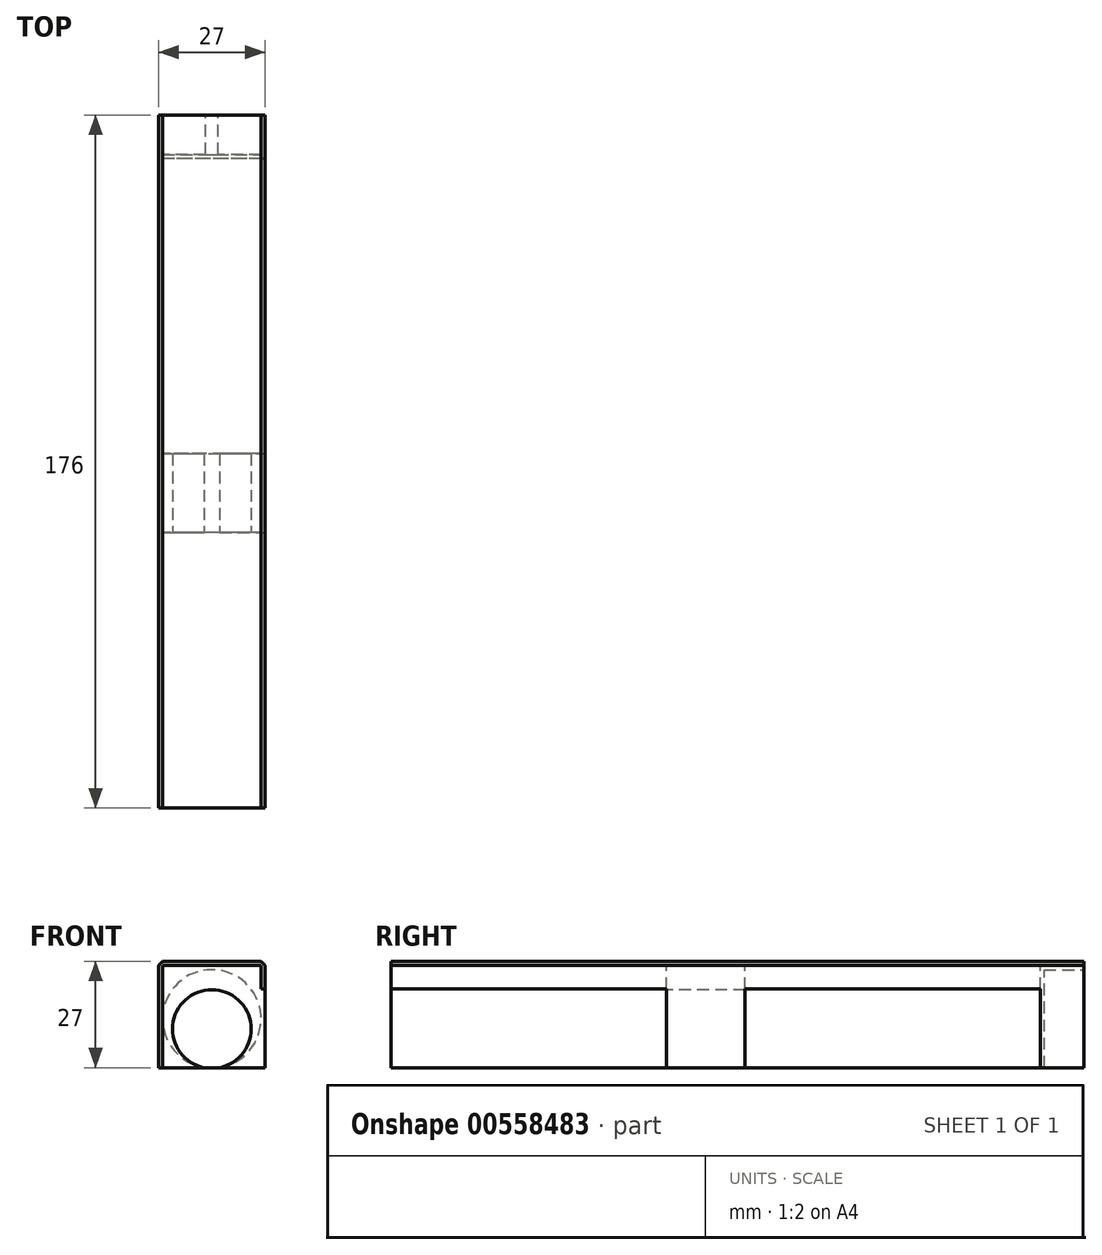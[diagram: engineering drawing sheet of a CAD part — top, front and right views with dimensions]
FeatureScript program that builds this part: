
annotation { "Feature Type Name" : "Feature", "Feature Type Description" : "" }
export const myFeature = defineFeature(function(context is Context, id is Id, definition is map)
    precondition{}
    {
        {
            var Q0;
            Q0=qCreatedBy(makeId("Front.planeOp"),FACE);
            var sketch = newSketch(context, id + "F0", { "sketchPlane" : qUnion([Q0])});
            skLineSegment(sketch, "E0", {"start": v(0, 0) * mm, "end": v(0, 27) * mm});
            skLineSegment(sketch, "E1", {"start": v(0, 27) * mm, "end": v(13.5, 27) * mm});
            skLineSegment(sketch, "E2", {"start": v(13.5, 27) * mm, "end": v(13.5, 26) * mm});
            skLineSegment(sketch, "E3", {"start": v(13.5, 26) * mm, "end": v(1, 26) * mm});
            skLineSegment(sketch, "E4", {"start": v(1, 26) * mm, "end": v(1, 0) * mm});
            skLineSegment(sketch, "E5", {"start": v(1, 0) * mm, "end": v(0, 0) * mm});
            skSolve(sketch);
        }
        {
            var Q0;
            Q0 = qSketchRegion(id + "F0", true);
            extrude(context, id + "F1", {"entities" : qUnion([Q0]), "depth" : 176 * mm, "offsetDistance" : 25 * mm});
        }
        {
            var Q0;
            Q0=makeQuery(id+"F1.opExtrude","SWEPT_BODY",BODY,{"disambiguationData":[OSD([sQuery(id+"F0.wireOp",EDGE,"E0"),sQuery(id+"F0.wireOp",EDGE,"E1"),sQuery(id+"F0.wireOp",EDGE,"E2"),sQuery(id+"F0.wireOp",EDGE,"E3"),sQuery(id+"F0.wireOp",EDGE,"E4"),sQuery(id+"F0.wireOp",EDGE,"E5")])]});
            var Q1;
            Q1=makeQuery(id+"F1.opExtrude","SWEPT_FACE",FACE,{"disambiguationData":[OSD([sQuery(id+"F0.wireOp",EDGE,"E2")])]});
            mirror(context, id + "F2", {"operationType" : NewBodyOperationType.ADD, "entities" : qUnion([Q0]), "mirrorPlane" : qUnion([Q1])});
        }
        {
            var Q0;
            {var subQ0=makeQuery(id+"F1.opExtrude","SWEPT_FACE",FACE,{"disambiguationData":[OSD([sQuery(id+"F0.wireOp",EDGE,"E3")])]});Q0=makeQuery(id+"F2.boolean.opBoolean","MERGE",FACE,{"derivedFrom":[subQ0,makeQuery(id+"F2.opPattern","COPY",FACE,{"derivedFrom":subQ0,"instanceName":"1"})]});}
            var sketch = newSketch(context, id + "F3", { "sketchPlane" : qUnion([Q0])});
            skLineSegment(sketch, "E6.bottom", {"start": v(26, 10) * mm, "end": v(1, 10) * mm});
            skLineSegment(sketch, "E6.top", {"start": v(26, 11) * mm, "end": v(1, 11) * mm});
            skLineSegment(sketch, "E6.left", {"start": v(26, 10) * mm, "end": v(26, 11) * mm});
            skLineSegment(sketch, "E6.right", {"start": v(1, 10) * mm, "end": v(1, 11) * mm});
            skSolve(sketch);
        }
        {
            var Q0;
            Q0 = qSketchRegion(id + "F3", true);
            var Q1;
            Q1=qCreatedBy(makeId("Front.planeOp"),FACE);
            var Q2;
            Q2=makeQuery(id+"F1.opExtrude","SWEPT_BODY",BODY,{"disambiguationData":[OSD([sQuery(id+"F0.wireOp",EDGE,"E0"),sQuery(id+"F0.wireOp",EDGE,"E1"),sQuery(id+"F0.wireOp",EDGE,"E2"),sQuery(id+"F0.wireOp",EDGE,"E3"),sQuery(id+"F0.wireOp",EDGE,"E4"),sQuery(id+"F0.wireOp",EDGE,"E5")])]});
            extrude(context, id + "F4", {"entities" : qUnion([Q0]), "operationType" : NewBodyOperationType.ADD, "depth" : 26 * mm, "endBoundEntityFace" : qUnion([Q1]), "endBoundEntityBody" : qUnion([Q2]), "offsetDistance" : 25 * mm});
        }
        {
            var Q0;
            Q0=makeQuery(id+"F4.opExtrude","SWEPT_FACE",FACE,{"disambiguationData":[OSD([sQuery(id+"F3.wireOp",EDGE,"E6.bottom")])]});
            var Q1;
            {var subQ0=makeQuery(id+"F1.opExtrude","CAP_FACE",FACE,{"disambiguationData":[OSD([sQuery(id+"F0.wireOp",EDGE,"E0"),sQuery(id+"F0.wireOp",EDGE,"E1"),sQuery(id+"F0.wireOp",EDGE,"E2"),sQuery(id+"F0.wireOp",EDGE,"E3"),sQuery(id+"F0.wireOp",EDGE,"E4"),sQuery(id+"F0.wireOp",EDGE,"E5")])],"isStart":true});Q1=makeQuery(id+"F2.boolean.opBoolean","MERGE",FACE,{"derivedFrom":[subQ0,makeQuery(id+"F2.opPattern","COPY",FACE,{"derivedFrom":subQ0,"instanceName":"1"})]});}
            extrude(context, id + "F5", {"entities" : qUnion([Q0]), "operationType" : NewBodyOperationType.ADD, "endBound" : BoundingType.UP_TO_SURFACE, "depth" : 25 * mm, "endBoundEntityFace" : qUnion([Q1]), "offsetDistance" : 25 * mm});
        }
        {
            var Q0;
            {var subQ0=sQuery(id+"F0.wireOp",EDGE,"E5");var subQ1=sQuery(id+"F0.wireOp",EDGE,"E4");var subQ2=sQuery(id+"F0.wireOp",EDGE,"E3");var subQ3=sQuery(id+"F0.wireOp",EDGE,"E2");var subQ4=sQuery(id+"F0.wireOp",EDGE,"E1");var subQ5=sQuery(id+"F0.wireOp",EDGE,"E0");var subQ6=makeQuery(id+"F1.opExtrude","CAP_FACE",FACE,{"disambiguationData":[OSD([subQ5,subQ4,subQ3,subQ2,subQ1,subQ0])],"isStart":true});Q0=makeQuery(id+"F5.boolean.opBoolean","MERGE",FACE,{"derivedFrom":[makeQuery(id+"F2.boolean.opBoolean","MERGE",FACE,{"derivedFrom":[subQ6,makeQuery(id+"F2.opPattern","COPY",FACE,{"derivedFrom":subQ6,"instanceName":"1"})]}),makeQuery(id+"F5.opExtrude","CAP_FACE",FACE,{"disambiguationData":[OSD([subQ5,subQ4,subQ3,subQ2,subQ1,subQ0])],"isStart":false})]});}
            var sketch = newSketch(context, id + "F6", { "sketchPlane" : qUnion([Q0])});
            skCircle(sketch, "E7", {"center": v(-13.5, 12.4) * mm, "radius": 12.5 * mm});
            skPoint(sketch, "E7.first.point", {"position": v(-15.1, 24.8) * mm});
            skPoint(sketch, "E7.second.point", {"position": v(-15.08, 0) * mm});
            skPoint(sketch, "E7.third.point", {"position": v(-11.92, 0) * mm});
            skSolve(sketch);
        }
        {
            var Q0;
            Q0 = qSketchRegion(id + "F6", true);
            extrude(context, id + "F7", {"entities" : qUnion([Q0]), "operationType" : NewBodyOperationType.REMOVE, "oppositeDirection" : true, "depth" : 10 * mm, "offsetDistance" : 25 * mm});
        }
        {
            var Q0;
            Q0=makeQuery(id+"F2.opPattern","COPY",FACE,{"derivedFrom":makeQuery(id+"F1.opExtrude","SWEPT_FACE",FACE,{"disambiguationData":[OSD([sQuery(id+"F0.wireOp",EDGE,"E0")])]}),"instanceName":"1"});
            var sketch = newSketch(context, id + "F8", { "sketchPlane" : qUnion([Q0])});
            skLineSegment(sketch, "E8.bottom", {"start": v(-11, 0) * mm, "end": v(-86, 0) * mm});
            skLineSegment(sketch, "E8.top", {"start": v(-11, 20) * mm, "end": v(-86, 20) * mm});
            skLineSegment(sketch, "E8.left", {"start": v(-11, 0) * mm, "end": v(-11, 20) * mm});
            skLineSegment(sketch, "E8.right", {"start": v(-86, 0) * mm, "end": v(-86, 20) * mm});
            skLineSegment(sketch, "E9.bottom", {"start": v(-106, 0) * mm, "end": v(-176, 0) * mm});
            skLineSegment(sketch, "E9.top", {"start": v(-106, 20) * mm, "end": v(-176, 20) * mm});
            skLineSegment(sketch, "E9.left", {"start": v(-106, 0) * mm, "end": v(-106, 20) * mm});
            skLineSegment(sketch, "E9.right", {"start": v(-176, 0) * mm, "end": v(-176, 20) * mm});
            skSolve(sketch);
        }
        {
            var Q0;
            Q0 = qSketchRegion(id + "F8", true);
            var Q1;
            {var subQ1=sQuery(id+"F0.wireOp",EDGE,"E4");var subQ6=sQuery(id+"F3.wireOp",EDGE,"E6.top");Q1=makeQuery(id+"F4.boolean.opBoolean","SPLIT",FACE,{"disambiguationData":[TD([makeQuery(id+"F4.opExtrude","SWEPT_FACE",FACE,{"disambiguationData":[OSD([subQ6])]})])],"derivedFrom":makeQuery(id+"F2.opPattern","COPY",FACE,{"derivedFrom":makeQuery(id+"F1.opExtrude","SWEPT_FACE",FACE,{"disambiguationData":[OSD([subQ1])]}),"instanceName":"1"})});}
            extrude(context, id + "F9", {"entities" : qUnion([Q0]), "operationType" : NewBodyOperationType.REMOVE, "endBound" : BoundingType.UP_TO_SURFACE, "oppositeDirection" : true, "depth" : 25 * mm, "endBoundEntityFace" : qUnion([Q1]), "offsetDistance" : 25 * mm});
        }
        {
            var Q0;
            {var subQ1=sQuery(id+"F0.wireOp",EDGE,"E3");var subQ4=makeQuery(id+"F1.opExtrude","SWEPT_FACE",FACE,{"disambiguationData":[OSD([subQ1])]});Q0=makeQuery(id+"F4.boolean.opBoolean","SPLIT",FACE,{"disambiguationData":[TD([makeQuery(id+"F4.opExtrude","SWEPT_FACE",FACE,{"disambiguationData":[OSD([sQuery(id+"F3.wireOp",EDGE,"E6.top")])]})])],"derivedFrom":makeQuery(id+"F2.boolean.opBoolean","MERGE",FACE,{"derivedFrom":[subQ4,makeQuery(id+"F2.opPattern","COPY",FACE,{"derivedFrom":subQ4,"instanceName":"1"})]})});}
            var sketch = newSketch(context, id + "F10", { "sketchPlane" : qUnion([Q0])});
            skLineSegment(sketch, "E10.bottom", {"start": v(26, 106) * mm, "end": v(1, 106) * mm});
            skLineSegment(sketch, "E10.top", {"start": v(26, 86) * mm, "end": v(1, 86) * mm});
            skLineSegment(sketch, "E10.left", {"start": v(26, 106) * mm, "end": v(26, 86) * mm});
            skLineSegment(sketch, "E10.right", {"start": v(1, 106) * mm, "end": v(1, 86) * mm});
            skSolve(sketch);
        }
        {
            var Q0;
            Q0 = qSketchRegion(id + "F10", true);
            var Q1;
            {var subQ0=sQuery(id+"F3.wireOp",EDGE,"E6.bottom");var subQ1=makeQuery(id+"F1.opExtrude","SWEPT_FACE",FACE,{"disambiguationData":[OSD([sQuery(id+"F0.wireOp",EDGE,"E5")])]});Q1=makeQuery(id+"F9.boolean.opBoolean","SPLIT",FACE,{"disambiguationData":[TD([makeQuery(id+"F2.opPattern","COPY",FACE,{"derivedFrom":makeQuery(id+"F1.opExtrude","SWEPT_FACE",FACE,{"disambiguationData":[OSD([sQuery(id+"F0.wireOp",EDGE,"E4")])]}),"instanceName":"1"})])],"derivedFrom":makeQuery(id+"F5.boolean.opBoolean","MERGE",FACE,{"derivedFrom":[makeQuery(id+"F4.boolean.opBoolean","MERGE",FACE,{"derivedFrom":[subQ1,makeQuery(id+"F2.opPattern","COPY",FACE,{"derivedFrom":subQ1,"instanceName":"1"}),makeQuery(id+"F4.opExtrude","CAP_FACE",FACE,{"disambiguationData":[OSD([subQ0,sQuery(id+"F3.wireOp",EDGE,"E6.top"),sQuery(id+"F3.wireOp",EDGE,"E6.left"),sQuery(id+"F3.wireOp",EDGE,"E6.right")])],"isStart":false})]}),makeQuery(id+"F5.opExtrude","SWEPT_FACE",FACE,{"disambiguationData":[OSD([subQ0]),TDD([makeQuery(id+"F4.opExtrude","CAP_EDGE",EDGE,{"disambiguationData":[OSD([subQ0])],"isStart":false})])]})]})});}
            extrude(context, id + "F11", {"entities" : qUnion([Q0]), "operationType" : NewBodyOperationType.ADD, "endBound" : BoundingType.UP_TO_SURFACE, "depth" : 25 * mm, "endBoundEntityFace" : qUnion([Q1]), "offsetDistance" : 25 * mm});
        }
        {
            var Q0;
            Q0=makeQuery(id+"F11.boolean.opBoolean","MERGE",FACE,{"derivedFrom":[makeQuery(id+"F9.boolean.opBoolean","COPY",FACE,{"derivedFrom":makeQuery(id+"F9.opExtrude","SWEPT_FACE",FACE,{"disambiguationData":[OSD([sQuery(id+"F8.wireOp",EDGE,"E9.left")])]})}),makeQuery(id+"F11.opExtrude","SWEPT_FACE",FACE,{"disambiguationData":[OSD([sQuery(id+"F10.wireOp",EDGE,"E10.bottom")])]})]});
            var sketch = newSketch(context, id + "F12", { "sketchPlane" : qUnion([Q0])});
            skCircle(sketch, "E11", {"center": v(13.5, 9.8) * mm, "radius": 10 * mm});
            skPoint(sketch, "E11.first.point", {"position": v(14.26, 19.77) * mm});
            skPoint(sketch, "E11.second.point", {"position": v(11.51, 0) * mm});
            skPoint(sketch, "E11.third.point", {"position": v(15.49, 0) * mm});
            skSolve(sketch);
        }
        {
            var Q0;
            Q0 = qSketchRegion(id + "F12", true);
            var Q1;
            Q1=makeQuery(id+"F11.boolean.opBoolean","MERGE",FACE,{"derivedFrom":[makeQuery(id+"F9.boolean.opBoolean","COPY",FACE,{"derivedFrom":makeQuery(id+"F9.opExtrude","SWEPT_FACE",FACE,{"disambiguationData":[OSD([sQuery(id+"F8.wireOp",EDGE,"E8.right")])]})}),makeQuery(id+"F11.opExtrude","SWEPT_FACE",FACE,{"disambiguationData":[OSD([sQuery(id+"F10.wireOp",EDGE,"E10.top")])]})]});
            extrude(context, id + "F13", {"entities" : qUnion([Q0]), "operationType" : NewBodyOperationType.REMOVE, "endBound" : BoundingType.UP_TO_SURFACE, "oppositeDirection" : true, "depth" : 25 * mm, "endBoundEntityFace" : qUnion([Q1]), "offsetDistance" : 25 * mm});
        }
        {
            var Q0;
            Q0=makeQuery(id+"F2.opPattern","COPY",EDGE,{"derivedFrom":makeQuery(id+"F1.opExtrude","SWEPT_EDGE",EDGE,{"disambiguationData":[OSD([sQuery(id+"F0.wireOp",EDGE,"E0"),sQuery(id+"F0.wireOp",EDGE,"E1")])]}),"instanceName":"1"});
            var Q1;
            Q1=makeQuery(id+"F1.opExtrude","SWEPT_EDGE",EDGE,{"disambiguationData":[OSD([sQuery(id+"F0.wireOp",EDGE,"E0"),sQuery(id+"F0.wireOp",EDGE,"E1")])]});
            chamfer(context, id + "F14", {"entities" : qUnion([Q0, Q1]), "width" : 1 * mm, "tangentPropagation" : true});
        }
    });
